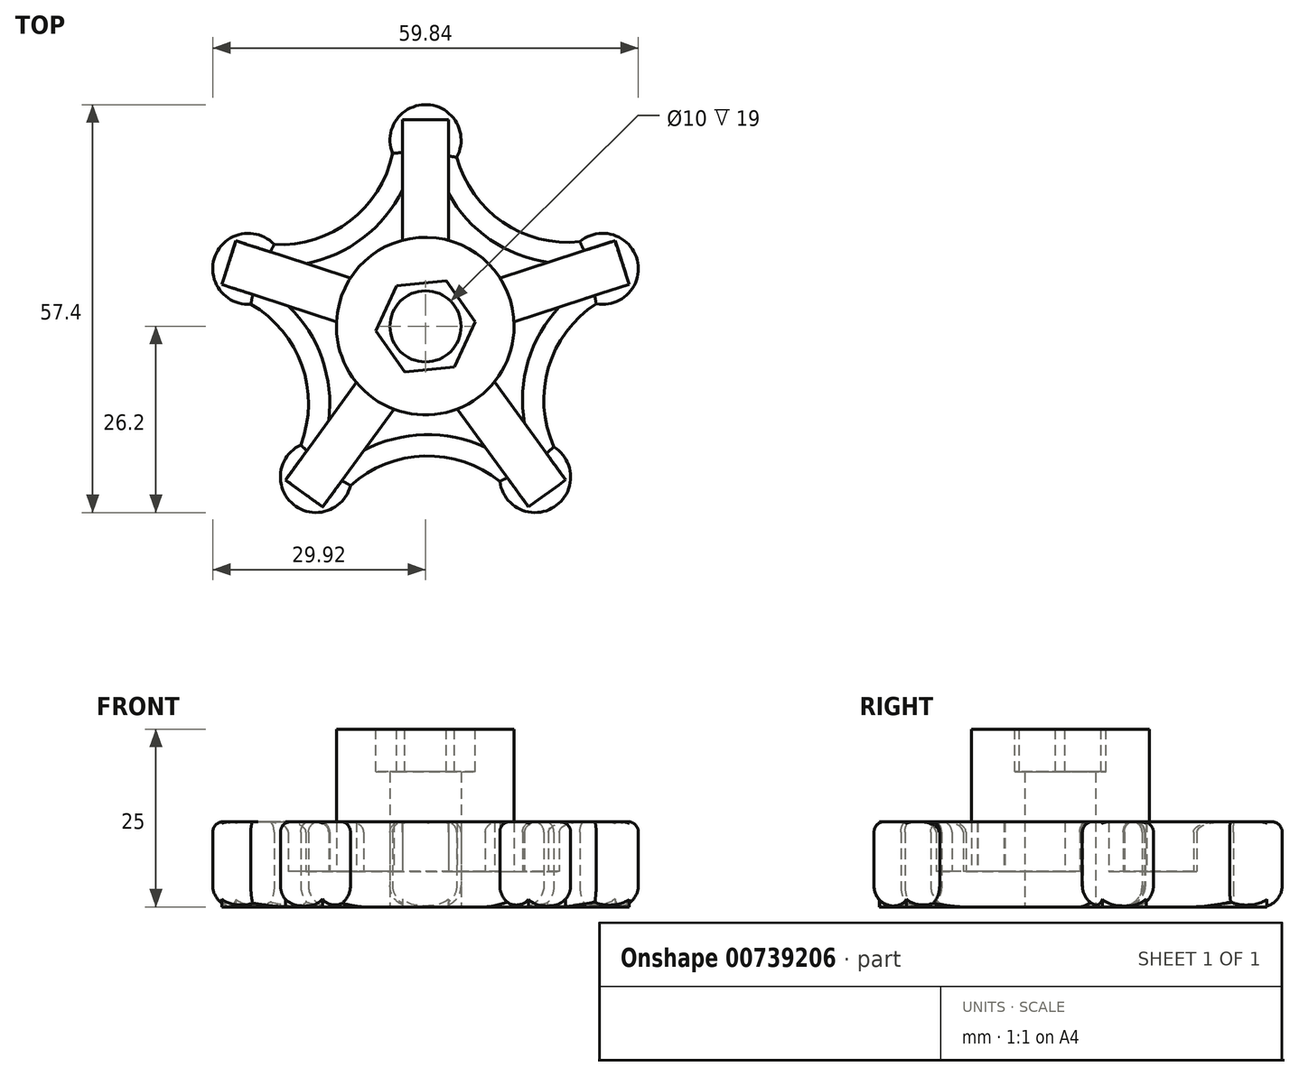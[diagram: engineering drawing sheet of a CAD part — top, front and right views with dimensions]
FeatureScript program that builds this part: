
annotation { "Feature Type Name" : "Feature", "Feature Type Description" : "" }
export const myFeature = defineFeature(function(context is Context, id is Id, definition is map)
    precondition{}
    {
        {
            var Q0;
            Q0=qCreatedBy(makeId("Top.planeOp"),FACE);
            var sketch = newSketch(context, id + "F0", { "sketchPlane" : qUnion([Q0])});
            skArc(sketch, "E0", {"start": v(4.39, 23.8) * mm, "mid": v(0.3, 31.2) * mm, "end": v(-4.64, 24.33) * mm});
            skArc(sketch, "E1.1.0", {"start": v(-21.29, 11.53) * mm, "mid": v(-29.58, 9.92) * mm, "end": v(-24.58, 3.1) * mm});
            skArc(sketch, "E1.2.0", {"start": v(-17.55, -16.68) * mm, "mid": v(-18.57, -25.07) * mm, "end": v(-10.55, -22.41) * mm});
            skArc(sketch, "E1.3.0", {"start": v(10.44, -21.84) * mm, "mid": v(18.1, -25.4) * mm, "end": v(18.05, -16.96) * mm});
            skArc(sketch, "E1.4.0", {"start": v(24, 3.18) * mm, "mid": v(29.76, 9.36) * mm, "end": v(21.71, 11.93) * mm});
            skPoint(sketch, "E1.center", {"position": v(0, 0) * mm});
            skArc(sketch, "E2", {"start": v(4.39, 23.8) * mm, "mid": v(10.85, 14.66) * mm, "end": v(21.71, 11.93) * mm});
            skArc(sketch, "E3.1.0", {"start": v(-21.29, 11.53) * mm, "mid": v(-10.6, 14.85) * mm, "end": v(-4.64, 24.33) * mm});
            skArc(sketch, "E3.2.0", {"start": v(-17.55, -16.68) * mm, "mid": v(-17.4, -5.48) * mm, "end": v(-24.58, 3.1) * mm});
            skArc(sketch, "E3.3.0", {"start": v(10.44, -21.84) * mm, "mid": v(-0.16, -18.24) * mm, "end": v(-10.55, -22.41) * mm});
            skArc(sketch, "E3.4.0", {"start": v(24, 3.18) * mm, "mid": v(17.3, -5.79) * mm, "end": v(18.05, -16.96) * mm});
            skSolve(sketch);
        }
        {
            var Q0;
            Q0=makeQuery(id+"F0.imprint","IMPRINT",FACE,{"disambiguationData":[TD([[makeQuery(id+"F0.imprint","IMPRINT",EDGE,{"derivedFrom":sQuery(id+"F0.wireOp",EDGE,"E0")}),1.0]])]});
            extrude(context, id + "F1", {"entities" : qUnion([Q0]), "depth" : 12 * mm, "offsetDistance" : 25 * mm});
        }
        {
            var Q0;
            Q0=makeQuery(id+"F1.opExtrude","CAP_FACE",FACE,{"disambiguationData":[OSD([sQuery(id+"F0.wireOp",EDGE,"E0"),sQuery(id+"F0.wireOp",EDGE,"E1.1.0"),sQuery(id+"F0.wireOp",EDGE,"E1.2.0"),sQuery(id+"F0.wireOp",EDGE,"E1.3.0"),sQuery(id+"F0.wireOp",EDGE,"E1.4.0"),sQuery(id+"F0.wireOp",EDGE,"E2"),sQuery(id+"F0.wireOp",EDGE,"E3.1.0"),sQuery(id+"F0.wireOp",EDGE,"E3.2.0"),sQuery(id+"F0.wireOp",EDGE,"E3.3.0"),sQuery(id+"F0.wireOp",EDGE,"E3.4.0")])],"isStart":false});
            shell(context, id + "F2", {"entities" : qUnion([Q0]), "thickness" : 3 * mm});
        }
        {
            var Q0;
            Q0=makeQuery(id+"F2.opShell","OFFSET_FACE",FACE,{"disambiguationData":[OSD([sQuery(id+"F0.wireOp",EDGE,"E0"),sQuery(id+"F0.wireOp",EDGE,"E1.1.0"),sQuery(id+"F0.wireOp",EDGE,"E1.2.0"),sQuery(id+"F0.wireOp",EDGE,"E1.3.0"),sQuery(id+"F0.wireOp",EDGE,"E1.4.0"),sQuery(id+"F0.wireOp",EDGE,"E2"),sQuery(id+"F0.wireOp",EDGE,"E3.1.0"),sQuery(id+"F0.wireOp",EDGE,"E3.2.0"),sQuery(id+"F0.wireOp",EDGE,"E3.3.0"),sQuery(id+"F0.wireOp",EDGE,"E3.4.0")])]});
            extrude(context, id + "F3", {"entities" : qUnion([Q0]), "operationType" : NewBodyOperationType.ADD, "depth" : 2 * mm, "offsetDistance" : 25 * mm});
        }
        {
            var Q0;
            Q0=qCreatedBy(makeId("Top.planeOp"),FACE);
            var sketch = newSketch(context, id + "F4", { "sketchPlane" : qUnion([Q0])});
            skCircle(sketch, "E4", {"center": v(-0.04, 0.04) * mm, "radius": 12.5 * mm});
            skSolve(sketch);
        }
        {
            var Q0;
            Q0 = qSketchRegion(id + "F4", true);
            extrude(context, id + "F5", {"entities" : qUnion([Q0]), "operationType" : NewBodyOperationType.ADD, "depth" : 25 * mm, "offsetDistance" : 25 * mm});
        }
        {
            var Q0;
            Q0=qCreatedBy(makeId("Top.planeOp"),FACE);
            var sketch = newSketch(context, id + "F6", { "sketchPlane" : qUnion([Q0])});
            skCircle(sketch, "E5", {"center": v(0, 0) * mm, "radius": 5 * mm});
            skSolve(sketch);
        }
        {
            var Q0;
            Q0=makeQuery(id+"F6.imprint","IMPRINT",FACE,{"disambiguationData":[TD([[makeQuery(id+"F6.imprint","IMPRINT",EDGE,{"derivedFrom":sQuery(id+"F6.wireOp",EDGE,"E5")}),1.0]])]});
            extrude(context, id + "F7", {"entities" : qUnion([Q0]), "depth" : 25 * mm, "offsetDistance" : 25 * mm});
        }
        {
            var Q0;
            Q0=makeQuery(id+"F1.opExtrude","CAP_EDGE",EDGE,{"disambiguationData":[OSD([sQuery(id+"F0.wireOp",EDGE,"E2")])],"isStart":false});
            var Q1;
            Q1=makeQuery(id+"F1.opExtrude","CAP_EDGE",EDGE,{"disambiguationData":[OSD([sQuery(id+"F0.wireOp",EDGE,"E1.4.0")])],"isStart":false});
            var Q2;
            Q2=makeQuery(id+"F1.opExtrude","CAP_EDGE",EDGE,{"disambiguationData":[OSD([sQuery(id+"F0.wireOp",EDGE,"E3.4.0")])],"isStart":false});
            var Q3;
            Q3=makeQuery(id+"F1.opExtrude","CAP_EDGE",EDGE,{"disambiguationData":[OSD([sQuery(id+"F0.wireOp",EDGE,"E1.3.0")])],"isStart":false});
            var Q4;
            Q4=makeQuery(id+"F1.opExtrude","CAP_EDGE",EDGE,{"disambiguationData":[OSD([sQuery(id+"F0.wireOp",EDGE,"E3.3.0")])],"isStart":false});
            var Q5;
            Q5=makeQuery(id+"F1.opExtrude","CAP_EDGE",EDGE,{"disambiguationData":[OSD([sQuery(id+"F0.wireOp",EDGE,"E1.2.0")])],"isStart":false});
            var Q6;
            Q6=makeQuery(id+"F1.opExtrude","CAP_EDGE",EDGE,{"disambiguationData":[OSD([sQuery(id+"F0.wireOp",EDGE,"E3.2.0")])],"isStart":false});
            var Q7;
            Q7=makeQuery(id+"F1.opExtrude","CAP_EDGE",EDGE,{"disambiguationData":[OSD([sQuery(id+"F0.wireOp",EDGE,"E1.1.0")])],"isStart":false});
            var Q8;
            Q8=makeQuery(id+"F1.opExtrude","CAP_EDGE",EDGE,{"disambiguationData":[OSD([sQuery(id+"F0.wireOp",EDGE,"E3.1.0")])],"isStart":false});
            var Q9;
            Q9=makeQuery(id+"F1.opExtrude","CAP_EDGE",EDGE,{"disambiguationData":[OSD([sQuery(id+"F0.wireOp",EDGE,"E0")])],"isStart":false});
            var Q10;
            {var subQ0=sQuery(id+"F0.wireOp",EDGE,"E2");Q10=makeQuery(id+"F2.opShell","OFFSET_EDGE",EDGE,{"disambiguationData":[OSD([subQ0]),TDD([makeQuery(id+"F1.opExtrude","CAP_EDGE",EDGE,{"disambiguationData":[OSD([subQ0])],"isStart":false})])]});}
            var Q11;
            {var subQ0=sQuery(id+"F0.wireOp",EDGE,"E1.4.0");Q11=makeQuery(id+"F2.opShell","OFFSET_EDGE",EDGE,{"disambiguationData":[OSD([subQ0]),TDD([makeQuery(id+"F1.opExtrude","CAP_EDGE",EDGE,{"disambiguationData":[OSD([subQ0])],"isStart":false})])]});}
            var Q12;
            {var subQ0=sQuery(id+"F0.wireOp",EDGE,"E3.4.0");Q12=makeQuery(id+"F2.opShell","OFFSET_EDGE",EDGE,{"disambiguationData":[OSD([subQ0]),TDD([makeQuery(id+"F1.opExtrude","CAP_EDGE",EDGE,{"disambiguationData":[OSD([subQ0])],"isStart":false})])]});}
            var Q13;
            {var subQ0=sQuery(id+"F0.wireOp",EDGE,"E1.3.0");Q13=makeQuery(id+"F2.opShell","OFFSET_EDGE",EDGE,{"disambiguationData":[OSD([subQ0]),TDD([makeQuery(id+"F1.opExtrude","CAP_EDGE",EDGE,{"disambiguationData":[OSD([subQ0])],"isStart":false})])]});}
            var Q14;
            {var subQ0=sQuery(id+"F0.wireOp",EDGE,"E3.3.0");Q14=makeQuery(id+"F2.opShell","OFFSET_EDGE",EDGE,{"disambiguationData":[OSD([subQ0]),TDD([makeQuery(id+"F1.opExtrude","CAP_EDGE",EDGE,{"disambiguationData":[OSD([subQ0])],"isStart":false})])]});}
            var Q15;
            {var subQ0=sQuery(id+"F0.wireOp",EDGE,"E1.2.0");Q15=makeQuery(id+"F2.opShell","OFFSET_EDGE",EDGE,{"disambiguationData":[OSD([subQ0]),TDD([makeQuery(id+"F1.opExtrude","CAP_EDGE",EDGE,{"disambiguationData":[OSD([subQ0])],"isStart":false})])]});}
            var Q16;
            {var subQ0=sQuery(id+"F0.wireOp",EDGE,"E3.2.0");Q16=makeQuery(id+"F2.opShell","OFFSET_EDGE",EDGE,{"disambiguationData":[OSD([subQ0]),TDD([makeQuery(id+"F1.opExtrude","CAP_EDGE",EDGE,{"disambiguationData":[OSD([subQ0])],"isStart":false})])]});}
            var Q17;
            {var subQ0=sQuery(id+"F0.wireOp",EDGE,"E1.1.0");Q17=makeQuery(id+"F2.opShell","OFFSET_EDGE",EDGE,{"disambiguationData":[OSD([subQ0]),TDD([makeQuery(id+"F1.opExtrude","CAP_EDGE",EDGE,{"disambiguationData":[OSD([subQ0])],"isStart":false})])]});}
            var Q18;
            {var subQ0=sQuery(id+"F0.wireOp",EDGE,"E3.1.0");Q18=makeQuery(id+"F2.opShell","OFFSET_EDGE",EDGE,{"disambiguationData":[OSD([subQ0]),TDD([makeQuery(id+"F1.opExtrude","CAP_EDGE",EDGE,{"disambiguationData":[OSD([subQ0])],"isStart":false})])]});}
            var Q19;
            {var subQ0=sQuery(id+"F0.wireOp",EDGE,"E0");Q19=makeQuery(id+"F2.opShell","OFFSET_EDGE",EDGE,{"disambiguationData":[OSD([subQ0]),TDD([makeQuery(id+"F1.opExtrude","CAP_EDGE",EDGE,{"disambiguationData":[OSD([subQ0])],"isStart":false})])]});}
            fillet(context, id + "F8", {"entities" : qUnion([Q0, Q1, Q2, Q3, Q4, Q5, Q6, Q7, Q8, Q9, Q10, Q11, Q12, Q13, Q14, Q15, Q16, Q17, Q18, Q19]), "radius" : 1.5 * mm, "tangentPropagation" : true, "allowEdgeOverflow" : false});
        }
        {
            var Q0;
            Q0=makeQuery(id+"F1.opExtrude","CAP_EDGE",EDGE,{"disambiguationData":[OSD([sQuery(id+"F0.wireOp",EDGE,"E2")])],"isStart":true});
            var Q1;
            Q1=makeQuery(id+"F1.opExtrude","CAP_EDGE",EDGE,{"disambiguationData":[OSD([sQuery(id+"F0.wireOp",EDGE,"E0")])],"isStart":true});
            var Q2;
            Q2=makeQuery(id+"F1.opExtrude","CAP_EDGE",EDGE,{"disambiguationData":[OSD([sQuery(id+"F0.wireOp",EDGE,"E3.1.0")])],"isStart":true});
            var Q3;
            Q3=makeQuery(id+"F1.opExtrude","CAP_EDGE",EDGE,{"disambiguationData":[OSD([sQuery(id+"F0.wireOp",EDGE,"E1.1.0")])],"isStart":true});
            var Q4;
            Q4=makeQuery(id+"F1.opExtrude","CAP_EDGE",EDGE,{"disambiguationData":[OSD([sQuery(id+"F0.wireOp",EDGE,"E3.2.0")])],"isStart":true});
            var Q5;
            Q5=makeQuery(id+"F1.opExtrude","CAP_EDGE",EDGE,{"disambiguationData":[OSD([sQuery(id+"F0.wireOp",EDGE,"E1.2.0")])],"isStart":true});
            var Q6;
            Q6=makeQuery(id+"F1.opExtrude","CAP_EDGE",EDGE,{"disambiguationData":[OSD([sQuery(id+"F0.wireOp",EDGE,"E3.3.0")])],"isStart":true});
            var Q7;
            Q7=makeQuery(id+"F1.opExtrude","CAP_EDGE",EDGE,{"disambiguationData":[OSD([sQuery(id+"F0.wireOp",EDGE,"E1.3.0")])],"isStart":true});
            var Q8;
            Q8=makeQuery(id+"F1.opExtrude","CAP_EDGE",EDGE,{"disambiguationData":[OSD([sQuery(id+"F0.wireOp",EDGE,"E3.4.0")])],"isStart":true});
            var Q9;
            Q9=makeQuery(id+"F1.opExtrude","CAP_EDGE",EDGE,{"disambiguationData":[OSD([sQuery(id+"F0.wireOp",EDGE,"E1.4.0")])],"isStart":true});
            fillet(context, id + "F9", {"entities" : qUnion([Q0, Q1, Q2, Q3, Q4, Q5, Q6, Q7, Q8, Q9]), "radius" : 3 * mm, "tangentPropagation" : true, "allowEdgeOverflow" : false});
        }
        {
            var Q0;
            Q0=makeQuery(id+"F5.opExtrude","CAP_FACE",FACE,{"disambiguationData":[OSD([sQuery(id+"F4.wireOp",EDGE,"E4")])],"isStart":false});
            var sketch = newSketch(context, id + "F10", { "sketchPlane" : qUnion([Q0])});
            skCircle(sketch, "E6.cCircle", {"center": v(0, 0) * mm, "radius": 6.1 * mm, "construction": true});
            skLineSegment(sketch, "E6.0", {"start": v(7.01, 0.67) * mm, "end": v(4.08, -5.74) * mm});
            skLineSegment(sketch, "E6.1", {"start": v(4.08, -5.74) * mm, "end": v(-2.93, -6.4) * mm});
            skLineSegment(sketch, "E6.2", {"start": v(-2.93, -6.4) * mm, "end": v(-7.01, -0.67) * mm});
            skLineSegment(sketch, "E6.3", {"start": v(-7.01, -0.67) * mm, "end": v(-4.08, 5.74) * mm});
            skLineSegment(sketch, "E6.4", {"start": v(-4.08, 5.74) * mm, "end": v(2.93, 6.4) * mm});
            skLineSegment(sketch, "E6.5", {"start": v(2.93, 6.4) * mm, "end": v(7.01, 0.67) * mm});
            skPoint(sketch, "E6.0.midPoint", {"position": v(5.55, -2.54) * mm});
            skSolve(sketch);
        }
        {
            var Q0;
            Q0=makeQuery(id+"F7.opExtrude","SWEPT_BODY",BODY,{"disambiguationData":[OSD([sQuery(id+"F6.wireOp",EDGE,"E5")])]});
            var Q1;
            Q1=makeQuery(id+"F1.opExtrude","SWEPT_BODY",BODY,{"disambiguationData":[OSD([sQuery(id+"F0.wireOp",EDGE,"E0"),sQuery(id+"F0.wireOp",EDGE,"E1.1.0"),sQuery(id+"F0.wireOp",EDGE,"E1.2.0"),sQuery(id+"F0.wireOp",EDGE,"E1.3.0"),sQuery(id+"F0.wireOp",EDGE,"E1.4.0"),sQuery(id+"F0.wireOp",EDGE,"E2"),sQuery(id+"F0.wireOp",EDGE,"E3.1.0"),sQuery(id+"F0.wireOp",EDGE,"E3.2.0"),sQuery(id+"F0.wireOp",EDGE,"E3.3.0"),sQuery(id+"F0.wireOp",EDGE,"E3.4.0")])]});
            booleanBodies(context, id + "F11", {"operationType" : BooleanOperationType.SUBTRACTION, "tools" : qUnion([Q0]), "targets" : qUnion([Q1])});
        }
        {
            var Q0;
            Q0 = qSketchRegion(id + "F10", true);
            extrude(context, id + "F12", {"entities" : qUnion([Q0]), "depth" : -6 * mm, "offsetDistance" : 25 * mm});
        }
        {
            var Q0;
            Q0=makeQuery(id+"F12.opExtrude","SWEPT_BODY",BODY,{"disambiguationData":[OSD([sQuery(id+"F10.wireOp",EDGE,"E6.0"),sQuery(id+"F10.wireOp",EDGE,"E6.1"),sQuery(id+"F10.wireOp",EDGE,"E6.2"),sQuery(id+"F10.wireOp",EDGE,"E6.3"),sQuery(id+"F10.wireOp",EDGE,"E6.4"),sQuery(id+"F10.wireOp",EDGE,"E6.5")])]});
            var Q1;
            Q1=makeQuery(id+"F1.opExtrude","SWEPT_BODY",BODY,{"disambiguationData":[OSD([sQuery(id+"F0.wireOp",EDGE,"E0"),sQuery(id+"F0.wireOp",EDGE,"E1.1.0"),sQuery(id+"F0.wireOp",EDGE,"E1.2.0"),sQuery(id+"F0.wireOp",EDGE,"E1.3.0"),sQuery(id+"F0.wireOp",EDGE,"E1.4.0"),sQuery(id+"F0.wireOp",EDGE,"E2"),sQuery(id+"F0.wireOp",EDGE,"E3.1.0"),sQuery(id+"F0.wireOp",EDGE,"E3.2.0"),sQuery(id+"F0.wireOp",EDGE,"E3.3.0"),sQuery(id+"F0.wireOp",EDGE,"E3.4.0")])]});
            booleanBodies(context, id + "F13", {"operationType" : BooleanOperationType.SUBTRACTION, "tools" : qUnion([Q0]), "targets" : qUnion([Q1])});
        }
        {
            var Q0;
            Q0=makeQuery(id+"F0.imprint","IMPRINT",FACE,{"disambiguationData":[TD([[makeQuery(id+"F0.imprint","IMPRINT",EDGE,{"derivedFrom":sQuery(id+"F0.wireOp",EDGE,"E0")}),1.0]])]});
            var sketch = newSketch(context, id + "F14", { "sketchPlane" : qUnion([Q0])});
            skLineSegment(sketch, "E7.bottom", {"start": v(3.22, 29.07) * mm, "end": v(-3.24, 29.07) * mm});
            skLineSegment(sketch, "E7.top", {"start": v(3.22, 8.02) * mm, "end": v(-3.24, 8.02) * mm});
            skLineSegment(sketch, "E7.left", {"start": v(3.22, 29.07) * mm, "end": v(3.22, 8.02) * mm});
            skLineSegment(sketch, "E7.right", {"start": v(-3.24, 29.07) * mm, "end": v(-3.24, 8.02) * mm});
            skLineSegment(sketch, "E8.1.0", {"start": v(-26.65, 12.04) * mm, "end": v(-6.63, 5.54) * mm});
            skLineSegment(sketch, "E8.1.1", {"start": v(-26.65, 12.04) * mm, "end": v(-28.65, 5.9) * mm});
            skLineSegment(sketch, "E8.1.2", {"start": v(-28.65, 5.9) * mm, "end": v(-8.63, -0.6) * mm});
            skLineSegment(sketch, "E8.1.3", {"start": v(-6.63, 5.54) * mm, "end": v(-8.63, -0.6) * mm});
            skLineSegment(sketch, "E8.2.0", {"start": v(-19.69, -21.63) * mm, "end": v(-7.32, -4.6) * mm});
            skLineSegment(sketch, "E8.2.1", {"start": v(-19.69, -21.63) * mm, "end": v(-14.46, -25.42) * mm});
            skLineSegment(sketch, "E8.2.2", {"start": v(-14.46, -25.42) * mm, "end": v(-2.1, -8.4) * mm});
            skLineSegment(sketch, "E8.2.3", {"start": v(-7.32, -4.6) * mm, "end": v(-2.1, -8.4) * mm});
            skLineSegment(sketch, "E8.3.0", {"start": v(14.48, -25.4) * mm, "end": v(2.11, -8.38) * mm});
            skLineSegment(sketch, "E8.3.1", {"start": v(14.48, -25.4) * mm, "end": v(19.7, -21.61) * mm});
            skLineSegment(sketch, "E8.3.2", {"start": v(19.7, -21.61) * mm, "end": v(7.34, -4.58) * mm});
            skLineSegment(sketch, "E8.3.3", {"start": v(2.11, -8.38) * mm, "end": v(7.34, -4.58) * mm});
            skLineSegment(sketch, "E8.4.0", {"start": v(28.64, 5.92) * mm, "end": v(8.62, -0.58) * mm});
            skLineSegment(sketch, "E8.4.1", {"start": v(28.64, 5.92) * mm, "end": v(26.64, 12.07) * mm});
            skLineSegment(sketch, "E8.4.2", {"start": v(26.64, 12.07) * mm, "end": v(6.63, 5.56) * mm});
            skLineSegment(sketch, "E8.4.3", {"start": v(8.62, -0.58) * mm, "end": v(6.63, 5.56) * mm});
            skPoint(sketch, "E8.center", {"position": v(0, 0) * mm});
            skSolve(sketch);
        }
        {
            var Q0;
            Q0 = qSketchRegion(id + "F14", true);
            extrude(context, id + "F15", {"entities" : qUnion([Q0]), "operationType" : NewBodyOperationType.ADD, "depth" : 12 * mm, "offsetDistance" : 25 * mm});
        }
    });
